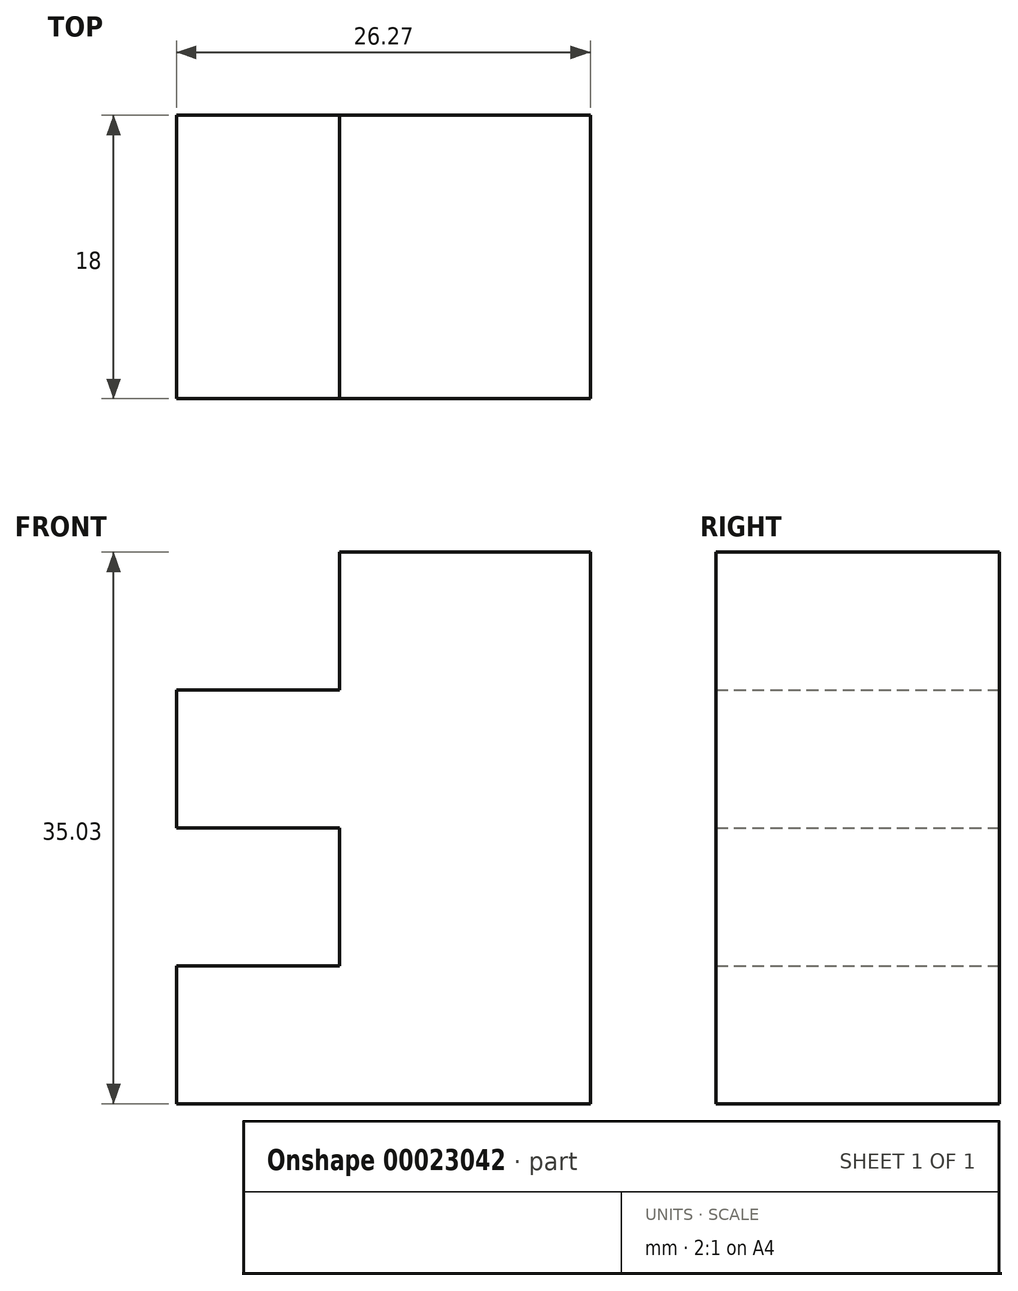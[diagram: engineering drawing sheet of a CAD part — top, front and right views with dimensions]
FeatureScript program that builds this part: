
annotation { "Feature Type Name" : "Feature", "Feature Type Description" : "" }
export const myFeature = defineFeature(function(context is Context, id is Id, definition is map)
    precondition{}
    {
        {
            var Q0;
            Q0=qCreatedBy(makeId("Front.planeOp"),FACE);
            var sketch = newSketch(context, id + "F0", { "sketchPlane" : qUnion([Q0])});
            skLineSegment(sketch, "E0", {"start": v(-62.63, 32.24) * mm, "end": v(-62.63, 41) * mm});
            skLineSegment(sketch, "E1", {"start": v(-52.28, 41) * mm, "end": v(-62.63, 41) * mm});
            skLineSegment(sketch, "E2", {"start": v(-52.28, 41) * mm, "end": v(-52.28, 49.76) * mm});
            skLineSegment(sketch, "E3", {"start": v(-62.63, 49.76) * mm, "end": v(-52.28, 49.76) * mm});
            skLineSegment(sketch, "E4", {"start": v(-62.63, 49.76) * mm, "end": v(-62.63, 58.51) * mm});
            skLineSegment(sketch, "E5", {"start": v(-52.28, 58.51) * mm, "end": v(-62.63, 58.51) * mm});
            skLineSegment(sketch, "E6", {"start": v(-52.28, 58.51) * mm, "end": v(-52.28, 67.27) * mm});
            skLineSegment(sketch, "E7", {"start": v(-52.28, 67.27) * mm, "end": v(-36.36, 67.27) * mm});
            skLineSegment(sketch, "E8", {"start": v(-36.36, 67.27) * mm, "end": v(-36.36, 32.24) * mm});
            skLineSegment(sketch, "E9", {"start": v(-36.36, 32.24) * mm, "end": v(-62.63, 32.24) * mm});
            skSolve(sketch);
        }
        {
            var Q0;
            Q0=makeQuery(id+"F0.imprint","IMPRINT",FACE,{"disambiguationData":[TD([[makeQuery(id+"F0.imprint","IMPRINT",EDGE,{"derivedFrom":sQuery(id+"F0.wireOp",EDGE,"E0")}),-1.0]])]});
            extrude(context, id + "F1", {"entities" : qUnion([Q0]), "depth" : 18 * mm});
        }
    });
